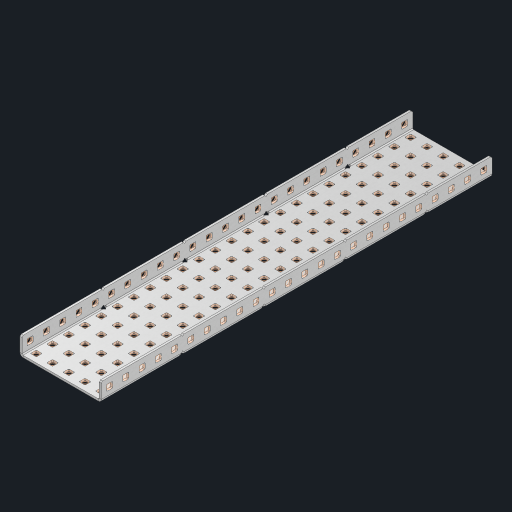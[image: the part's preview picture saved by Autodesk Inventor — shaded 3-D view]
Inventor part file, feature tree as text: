
AUTODESK INVENTOR PART (.ipt)
format: ipt  version: 2023 (Build 270158000, 158)  size: 1,890,304 bytes
history: native  units: in
note: dims shown in document units (in); Inventor stores cm internally (conversion verified against a paired STEP export)
features: other x173, extrude x167, sheet_metal_op x10, sketch x8, mirror x1, pattern_linear x1, chamfer x1
ambient origin geometry x8: Origin, YZ Plane, XZ Plane, XY Plane, X Axis, Y Axis, Z Axis, Center Point
bodies: Solid1 (feature_tree), Body (feature_tree)
feature tree (361):
  other  "Flange Pattern Plane"
  sheet_metal_op  "Flange Pattern"
  sheet_metal_op  "Body Pattern"
  other  "Arc Length"
  mirror  "Notch Mirror"
  pattern_linear  "Notch Pattern"  Spacing1=0.25in  [1 undecoded]
  chamfer  "End Chamfer"
  extrude  "Half Cut"  Depth=0.0625in
  sketch  "Sketch1"  dims[d0=2.5in]
  other  "Plate1"
  sketch  "Sketch2"  dims[d1=12.0in]
  other  "Plate2"
  sheet_metal_op  "Bend1"
  sheet_metal_op  "Corner1"
  sketch  "Sketch3"  dims[d2=0.0625in]
  other  "Flange Pattern Sketch"
  sketch  "Sketch7"  dims[d3=0.0625in]
  other  "Srf1"
  other  "Srf2"
  sketch  "Sketch8"  dims[d4=0.0312in]
  sketch  "Sketch9"  dims[d5=0.125in]
  other  "Srf91"
  sheet_metal_op  "Body Pattern Sketch"
  other  "Srf92"
  sketch  "Sketch13"  dims[d6=0.0625in]
  sketch  "Sketch14"  dims[d7=0.5in d8=90.0deg d9=0.0312in d10=0.25in d11=0.0625in d12=0.0625in d16=0.182in d17=0.02in d18=0.0625in d19=0.0in d20=0.25in d21=0.25in d46=0.172in d47=1.0in d48=0.0in d49=0.182in d50=0.02in d51=0.25in d52=0.25in d53=0.0625in d54=0.0in d55=0.172in d56=1.0in d57=0.0in d60=9.4488in d62=0.5in d63=1.9685in d65=0.5in d85=0.1473in d86=0.1782in d88=0.04in d89=0.0625in d90=0.0in d91=0.04in d92=0.0491in d95=2.5in d96=0.04in d97=0.25in d98=45.0deg d101=0.0in d102=2.497in d131=2.5in d132=9.4488in d134=0.5in d139=0.5in]
  other  "Srf856"
  other  "Srf1310"
  other  "Srf1311"
  other  "Srf1312"
  other  "Srf1376"
  other  "Srf1377"
  other  "Srf1728"
  other  "Srf1755"
  other  "Srf1878"
  other  "Srf1879"
  other  "Srf1880"
  other  "Srf1881"
  other  "Srf1882"
  other  "Srf1883"
  other  "Srf1884"
  other  "Srf1885"
  other  "Srf1886"
  other  "Srf1887"
  other  "Srf1888"
  other  "Srf1889"
  other  "Srf1890"
  other  "Srf1891"
  other  "Srf1892"
  other  "Srf1893"
  other  "Srf1894"
  other  "Srf1895"
  other  "Srf1896"
  other  "Srf1897"
  other  "Srf1898"
  other  "Srf1899"
  other  "Srf1900"
  other  "Srf1901"
  other  "Srf1902"
  other  "Srf1903"
  other  "Srf1904"
  other  "Srf1905"
  other  "Srf1906"
  other  "Srf1942"
  other  "Srf1943"
  other  "Srf1944"
  other  "Srf1945"
  other  "Srf1946"
  other  "Srf1947"
  other  "Srf1948"
  other  "Srf1949"
  other  "Srf1950"
  other  "Srf1951"
  other  "Srf1952"
  other  "Srf1953"
  other  "Srf1954"
  other  "Srf1955"
  other  "Srf1956"
  other  "Srf1957"
  other  "Srf1958"
  other  "Srf1959"
  other  "Srf1960"
  other  "Srf1961"
  other  "Srf1962"
  other  "Srf1963"
  other  "Srf1964"
  other  "Srf1965"
  other  "Srf1966"
  other  "Srf1967"
  other  "Srf1968"
  other  "Srf1969"
  other  "Srf1970"
  other  "Srf2111"
  other  "Srf2112"
  other  "Srf2113"
  other  "Srf2114"
  other  "Srf2115"
  other  "Srf2116"
  other  "Srf2117"
  other  "Srf2118"
  other  "Srf2119"
  other  "Srf2120"
  other  "Srf2121"
  other  "Srf2122"
  other  "Srf2123"
  other  "Srf2146"
  other  "Srf2147"
  other  "Srf2148"
  other  "Srf2149"
  other  "Srf2150"
  other  "Srf2151"
  other  "Srf2152"
  other  "Srf2153"
  other  "Srf2154"
  other  "Srf2155"
  other  "Srf2156"
  other  "Srf2157"
  other  "Srf2158"
  other  "Srf2159"
  other  "Srf2160"
  other  "Srf2161"
  other  "Srf2162"
  other  "Srf2163"
  other  "Srf2164"
  other  "Srf2165"
  other  "Srf2166"
  other  "Srf2167"
  other  "Srf2168"
  other  "Srf2169"
  other  "Srf2170"
  other  "Srf2171"
  other  "Srf2172"
  other  "Srf2173"
  other  "Srf2174"
  other  "Srf2175"
  other  "Srf2176"
  other  "Srf2177"
  other  "Srf2178"
  other  "Srf2179"
  other  "Srf2180"
  other  "Srf2181"
  other  "Srf2182"
  other  "Srf2183"
  other  "Srf2184"
  other  "Srf2185"
  other  "Srf2186"
  other  "Srf2187"
  other  "Srf2188"
  other  "Srf2189"
  other  "Srf2190"
  other  "Srf2191"
  other  "Srf2192"
  other  "Srf2193"
  other  "Srf2194"
  other  "Srf2195"
  other  "Srf2196"
  other  "Srf2197"
  other  "Srf2198"
  other  "Srf2199"
  other  "Srf2200"
  other  "Srf2201"
  other  "Srf2202"
  other  "Srf2203"
  other  "Srf2204"
  other  "Srf2205"
  other  "Srf2206"
  other  "Srf2207"
  other  "Srf2208"
  other  "Srf2209"
  other  "Srf2210"
  other  "Srf2211"
  other  "Srf2212"
  other  "Srf2213"
  other  "Srf2214"
  other  "Srf2215"
  other  "Srf2216"
  other  "Srf2217"
  other  "Srf2218"
  other  "Srf2219"
  other  "Srf2220"
  other  "Srf2221"
  other  "Srf2222"
  other  "Srf2223"
  other  "Srf2224"
  other  "Srf2225"
  other  "Srf2226"
  other  "Srf2227"
  other  "Srf2228"
  other  "Srf2229"
  other  "Srf2230"
  sheet_metal_op  "Flange Stamp"
  sheet_metal_op  "Flange Circle"
  sheet_metal_op  "Body Stamp"
  sheet_metal_op  "Body Circle"
  sheet_metal_op  "Notch"
  extrude  "ExtrusionSrf2"  Depth=0.0625in
  extrude  "ExtrusionSrf92"  Depth=2.5in
  extrude  "ExtrusionSrf856"  Depth=0.02in
  extrude  "ExtrusionSrf1310"  Depth=0.0625in
  extrude  "ExtrusionSrf1311"  TaperAngle=0.0deg  [1 undecoded]
  extrude  "ExtrusionSrf1312"  Depth=0.25in
  extrude  "ExtrusionSrf1376"  Depth=0.25in
  extrude  "ExtrusionSrf1377"  Depth=2.5in
  extrude  "ExtrusionSrf1728"  Depth=2.5in TaperAngle=0.0deg
  extrude  "ExtrusionSrf1755"  Depth=2.5in
  extrude  "ExtrusionSrf1878"  Depth=0.02in
  extrude  "ExtrusionSrf1879"  Depth=0.25in
  extrude  "ExtrusionSrf1880"  Depth=0.25in
  extrude  "ExtrusionSrf1881"  Depth=0.0625in
  extrude  "ExtrusionSrf1882"  TaperAngle=0.0deg  [1 undecoded]
  extrude  "ExtrusionSrf1883"  Depth=2.5in
  extrude  "ExtrusionSrf1884"  Depth=2.5in TaperAngle=0.0deg
  extrude  "ExtrusionSrf1885"  Depth=2.5in
  extrude  "ExtrusionSrf1886"  Depth=2.5in
  extrude  "ExtrusionSrf1887"  Depth=2.5in
  extrude  "ExtrusionSrf1888"  Depth=2.5in
  extrude  "ExtrusionSrf1889"  Depth=2.5in
  extrude  "ExtrusionSrf1890"  Depth=0.0625in
  extrude  "ExtrusionSrf1891"  TaperAngle=0.0deg  [1 undecoded]
  extrude  "ExtrusionSrf1892"  Depth=2.5in
  extrude  "ExtrusionSrf1893"  Depth=2.5in
  extrude  "ExtrusionSrf1894"  Depth=2.5in
  extrude  "ExtrusionSrf1895"  Depth=0.25in TaperAngle=45.0deg
  extrude  "ExtrusionSrf1896"  TaperAngle=0.0deg  [1 undecoded]
  extrude  "ExtrusionSrf1897"  Depth=2.5in
  extrude  "ExtrusionSrf1898"  Depth=2.5in
  extrude  "ExtrusionSrf1899"  Depth=2.5in
  extrude  "ExtrusionSrf1900"  Depth=2.5in
  extrude  "ExtrusionSrf1901"  Depth=2.5in
  extrude  "ExtrusionSrf1902"  [1 undecoded]
  extrude  "ExtrusionSrf1903"  [1 undecoded]
  extrude  "ExtrusionSrf1904"  [1 undecoded]
  extrude  "ExtrusionSrf1905"  [1 undecoded]
  extrude  "ExtrusionSrf1906"  [1 undecoded]
  extrude  "ExtrusionSrf1942"  [1 undecoded]
  extrude  "ExtrusionSrf1943"  [1 undecoded]
  extrude  "ExtrusionSrf1944"  [1 undecoded]
  extrude  "ExtrusionSrf1945"  [1 undecoded]
  extrude  "ExtrusionSrf1946"  [1 undecoded]
  extrude  "ExtrusionSrf1947"  [1 undecoded]
  extrude  "ExtrusionSrf1948"  [1 undecoded]
  extrude  "ExtrusionSrf1949"  [1 undecoded]
  extrude  "ExtrusionSrf1950"  [1 undecoded]
  extrude  "ExtrusionSrf1951"  [1 undecoded]
  extrude  "ExtrusionSrf1952"  [1 undecoded]
  extrude  "ExtrusionSrf1953"  [1 undecoded]
  extrude  "ExtrusionSrf1954"  [1 undecoded]
  extrude  "ExtrusionSrf1955"  [1 undecoded]
  extrude  "ExtrusionSrf1956"  [1 undecoded]
  extrude  "ExtrusionSrf1957"  [1 undecoded]
  extrude  "ExtrusionSrf1958"  [1 undecoded]
  extrude  "ExtrusionSrf1959"  [1 undecoded]
  extrude  "ExtrusionSrf1960"  [1 undecoded]
  extrude  "ExtrusionSrf1961"  [1 undecoded]
  extrude  "ExtrusionSrf1962"  [1 undecoded]
  extrude  "ExtrusionSrf1963"  [1 undecoded]
  extrude  "ExtrusionSrf1964"  [1 undecoded]
  extrude  "ExtrusionSrf1965"  [1 undecoded]
  extrude  "ExtrusionSrf1966"  [1 undecoded]
  extrude  "ExtrusionSrf1967"  [1 undecoded]
  extrude  "ExtrusionSrf1968"  [1 undecoded]
  extrude  "ExtrusionSrf1969"  [1 undecoded]
  extrude  "ExtrusionSrf1970"  [1 undecoded]
  extrude  "ExtrusionSrf2111"  [1 undecoded]
  extrude  "ExtrusionSrf2112"  [1 undecoded]
  extrude  "ExtrusionSrf2113"  [1 undecoded]
  extrude  "ExtrusionSrf2114"  [1 undecoded]
  extrude  "ExtrusionSrf2115"  [1 undecoded]
  extrude  "ExtrusionSrf2116"  [1 undecoded]
  extrude  "ExtrusionSrf2117"  [1 undecoded]
  extrude  "ExtrusionSrf2118"  [1 undecoded]
  extrude  "ExtrusionSrf2119"  [1 undecoded]
  extrude  "ExtrusionSrf2120"  [1 undecoded]
  extrude  "ExtrusionSrf2121"  [1 undecoded]
  extrude  "ExtrusionSrf2122"  [1 undecoded]
  extrude  "ExtrusionSrf2123"  [1 undecoded]
  extrude  "ExtrusionSrf2146"  [1 undecoded]
  extrude  "ExtrusionSrf2147"  [1 undecoded]
  extrude  "ExtrusionSrf2148"  [1 undecoded]
  extrude  "ExtrusionSrf2149"  [1 undecoded]
  extrude  "ExtrusionSrf2150"  [1 undecoded]
  extrude  "ExtrusionSrf2151"  [1 undecoded]
  extrude  "ExtrusionSrf2152"  [1 undecoded]
  extrude  "ExtrusionSrf2153"  [1 undecoded]
  extrude  "ExtrusionSrf2154"  [1 undecoded]
  extrude  "ExtrusionSrf2155"  [1 undecoded]
  extrude  "ExtrusionSrf2156"  [1 undecoded]
  extrude  "ExtrusionSrf2157"  [1 undecoded]
  extrude  "ExtrusionSrf2158"  [1 undecoded]
  extrude  "ExtrusionSrf2159"  [1 undecoded]
  extrude  "ExtrusionSrf2160"  [1 undecoded]
  extrude  "ExtrusionSrf2161"  [1 undecoded]
  extrude  "ExtrusionSrf2162"  [1 undecoded]
  extrude  "ExtrusionSrf2163"  [1 undecoded]
  extrude  "ExtrusionSrf2164"  [1 undecoded]
  extrude  "ExtrusionSrf2165"  [1 undecoded]
  extrude  "ExtrusionSrf2166"  [1 undecoded]
  extrude  "ExtrusionSrf2167"  [1 undecoded]
  extrude  "ExtrusionSrf2168"  [1 undecoded]
  extrude  "ExtrusionSrf2169"  [1 undecoded]
  extrude  "ExtrusionSrf2170"  [1 undecoded]
  extrude  "ExtrusionSrf2171"  [1 undecoded]
  extrude  "ExtrusionSrf2172"  [1 undecoded]
  extrude  "ExtrusionSrf2173"  [1 undecoded]
  extrude  "ExtrusionSrf2174"  [1 undecoded]
  extrude  "ExtrusionSrf2175"  [1 undecoded]
  extrude  "ExtrusionSrf2176"  [1 undecoded]
  extrude  "ExtrusionSrf2177"  [1 undecoded]
  extrude  "ExtrusionSrf2178"  [1 undecoded]
  extrude  "ExtrusionSrf2179"  [1 undecoded]
  extrude  "ExtrusionSrf2180"  [1 undecoded]
  extrude  "ExtrusionSrf2181"  [1 undecoded]
  extrude  "ExtrusionSrf2182"  [1 undecoded]
  extrude  "ExtrusionSrf2183"  [1 undecoded]
  extrude  "ExtrusionSrf2184"  [1 undecoded]
  extrude  "ExtrusionSrf2185"  [1 undecoded]
  extrude  "ExtrusionSrf2186"  [1 undecoded]
  extrude  "ExtrusionSrf2187"  [1 undecoded]
  extrude  "ExtrusionSrf2188"  [1 undecoded]
  extrude  "ExtrusionSrf2189"  [1 undecoded]
  extrude  "ExtrusionSrf2190"  [1 undecoded]
  extrude  "ExtrusionSrf2191"  [1 undecoded]
  extrude  "ExtrusionSrf2192"  [1 undecoded]
  extrude  "ExtrusionSrf2193"  [1 undecoded]
  extrude  "ExtrusionSrf2194"  [1 undecoded]
  extrude  "ExtrusionSrf2195"  [1 undecoded]
  extrude  "ExtrusionSrf2196"  [1 undecoded]
  extrude  "ExtrusionSrf2197"  [1 undecoded]
  extrude  "ExtrusionSrf2198"  [1 undecoded]
  extrude  "ExtrusionSrf2199"  [1 undecoded]
  extrude  "ExtrusionSrf2200"  [1 undecoded]
  extrude  "ExtrusionSrf2201"  [1 undecoded]
  extrude  "ExtrusionSrf2202"  [1 undecoded]
  extrude  "ExtrusionSrf2203"  [1 undecoded]
  extrude  "ExtrusionSrf2204"  [1 undecoded]
  extrude  "ExtrusionSrf2205"  [1 undecoded]
  extrude  "ExtrusionSrf2206"  [1 undecoded]
  extrude  "ExtrusionSrf2207"  [1 undecoded]
  extrude  "ExtrusionSrf2208"  [1 undecoded]
  extrude  "ExtrusionSrf2209"  [1 undecoded]
  extrude  "ExtrusionSrf2210"  [1 undecoded]
  extrude  "ExtrusionSrf2211"  [1 undecoded]
  extrude  "ExtrusionSrf2212"  [1 undecoded]
  extrude  "ExtrusionSrf2213"  [1 undecoded]
  extrude  "ExtrusionSrf2214"  [1 undecoded]
  extrude  "ExtrusionSrf2215"  [1 undecoded]
  extrude  "ExtrusionSrf2216"  [1 undecoded]
  extrude  "ExtrusionSrf2217"  [1 undecoded]
  extrude  "ExtrusionSrf2218"  [1 undecoded]
  extrude  "ExtrusionSrf2219"  [1 undecoded]
  extrude  "ExtrusionSrf2220"  [1 undecoded]
  extrude  "ExtrusionSrf2221"  [1 undecoded]
  extrude  "ExtrusionSrf2222"  [1 undecoded]
  extrude  "ExtrusionSrf2223"  [1 undecoded]
  extrude  "ExtrusionSrf2224"  [1 undecoded]
  extrude  "ExtrusionSrf2225"  [1 undecoded]
  extrude  "ExtrusionSrf2226"  [1 undecoded]
  extrude  "ExtrusionSrf2227"  [1 undecoded]
  extrude  "ExtrusionSrf2228"  [1 undecoded]
  extrude  "ExtrusionSrf2229"  [1 undecoded]
  extrude  "ExtrusionSrf2230"  [1 undecoded]
note: 137 required parameter values undecoded (feature->parameter linkage not recoverable at this tier; creation-order binding heuristic only, values carry confidence <= 0.55)
